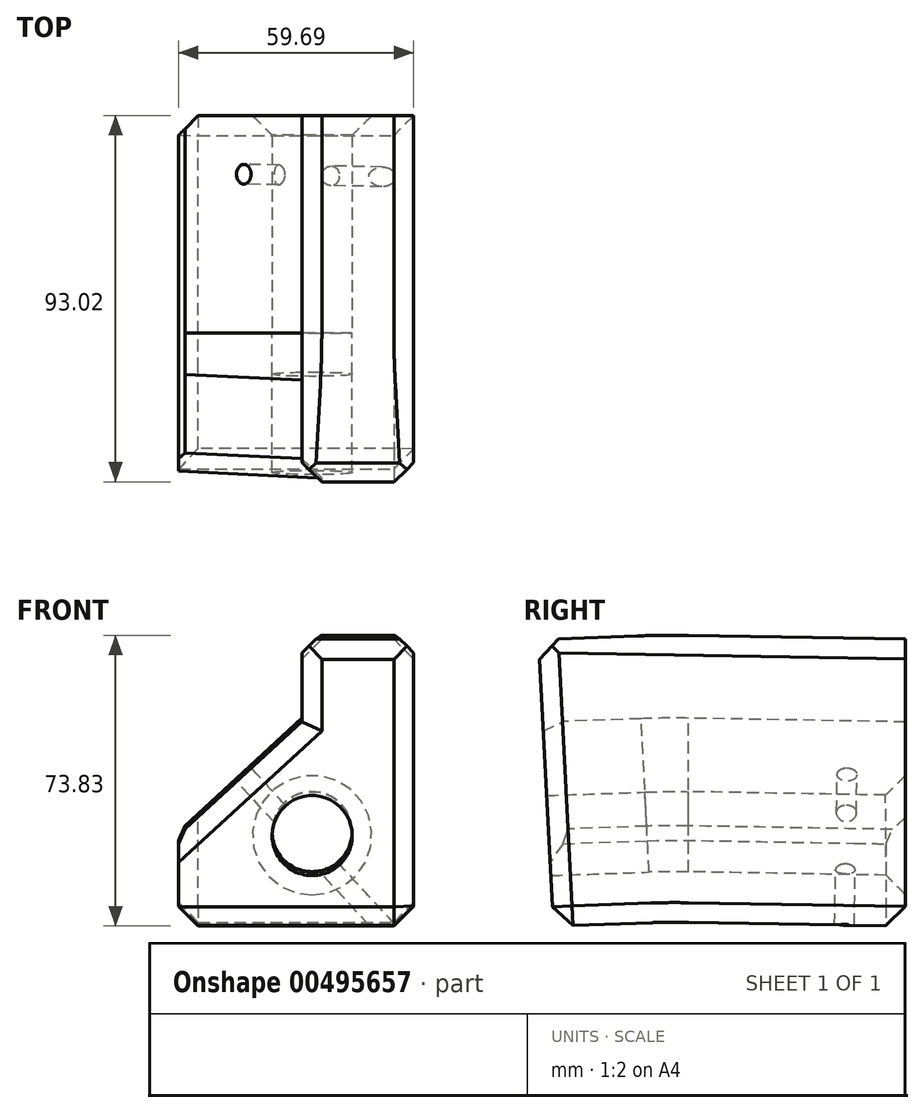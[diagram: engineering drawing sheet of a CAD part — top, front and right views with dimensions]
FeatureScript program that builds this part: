
annotation { "Feature Type Name" : "Feature", "Feature Type Description" : "" }
export const myFeature = defineFeature(function(context is Context, id is Id, definition is map)
    precondition{}
    {
        {
            var Q0;
            Q0=qCreatedBy(makeId("Front.planeOp"),FACE);
            var sketch = newSketch(context, id + "F0", { "sketchPlane" : qUnion([Q0])});
            skLineSegment(sketch, "E0", {"start": v(0, 0) * mm, "end": v(31.39, 28.85) * mm});
            skLineSegment(sketch, "E1", {"start": v(31.39, 28.85) * mm, "end": v(31.39, 49.9) * mm});
            skLineSegment(sketch, "E2", {"start": v(31.39, 49.9) * mm, "end": v(59.69, 49.9) * mm});
            skLineSegment(sketch, "E3", {"start": v(59.69, 49.9) * mm, "end": v(59.69, -23.04) * mm});
            skLineSegment(sketch, "E4", {"start": v(59.69, -23.04) * mm, "end": v(0, -23.04) * mm});
            skLineSegment(sketch, "E5", {"start": v(0, -23.04) * mm, "end": v(0, 0) * mm});
            skCircle(sketch, "E6", {"center": v(33.93, 0) * mm, "radius": 10.17 * mm});
            skSolve(sketch);
        }
        {
            var Q0;
            Q0=qCreatedBy(makeId("Right.planeOp"),FACE);
            var sketch = newSketch(context, id + "F1", { "sketchPlane" : qUnion([Q0])});
            skLineSegment(sketch, "E7", {"start": v(0, 0) * mm, "end": v(-55.22, 0.96) * mm});
            skLineSegment(sketch, "E8", {"start": v(-65.69, 0.87) * mm, "end": v(-90.67, 0) * mm});
            skPoint(sketch, "E9.visualSharp", {"position": v(-60.46, 1.06) * mm});
            skArc(sketch, "E9.filletArc", {"start": v(-55.22, 0.96) * mm, "mid": v(-60.46, 0.99) * mm, "end": v(-65.69, 0.87) * mm});
            skSolve(sketch);
        }
        {
            var Q0;
            Q0=makeQuery(id+"F0.imprint","IMPRINT",FACE,{"disambiguationData":[TD([[makeQuery(id+"F0.imprint","IMPRINT",EDGE,{"derivedFrom":sQuery(id+"F0.wireOp",EDGE,"E0")}),-1.0]])]});
            var Q1;
            Q1 = qConstructionFilter(qBodyType(qCreatedBy(id + "F1" ,EDGE), BodyType.WIRE), ConstructionObject.NO);
            sweep(context, id + "F2", {"profiles" : qUnion([Q0]), "path" : qUnion([Q1])});
        }
        {
            var Q0;
            Q0=makeQuery(id+"F2.opSweep","SWEPT_FACE",FACE,{"disambiguationData":[OSD([sQuery(id+"F0.wireOp",EDGE,"E5"),sQuery(id+"F1.wireOp",EDGE,"E7")])]});
            var sketch = newSketch(context, id + "F3", { "sketchPlane" : qUnion([Q0])});
            skCircle(sketch, "E10", {"center": v(22.5, -15.15) * mm, "radius": 2.5 * mm});
            skSolve(sketch);
        }
        {
            var Q0;
            Q0=makeQuery(id+"F3.imprint","IMPRINT",FACE,{"disambiguationData":[TD([[makeQuery(id+"F3.imprint","IMPRINT",EDGE,{"derivedFrom":sQuery(id+"F3.wireOp",EDGE,"E10")}),1.0]])]});
            extrude(context, id + "F4", {"entities" : qUnion([Q0]), "operationType" : NewBodyOperationType.REMOVE, "oppositeDirection" : true, "depth" : 200 * mm});
        }
        {
            var Q0;
            Q0=makeQuery(id+"F2.opSweep","SWEPT_EDGE",EDGE,{"disambiguationData":[OSD([sQuery(id+"F0.wireOp",EDGE,"E1"),sQuery(id+"F0.wireOp",EDGE,"E2"),sQuery(id+"F1.wireOp",EDGE,"E7")])]});
            var Q1;
            Q1=makeQuery(id+"F2.opSweep","SWEPT_EDGE",EDGE,{"disambiguationData":[OSD([sQuery(id+"F0.wireOp",EDGE,"E0"),sQuery(id+"F0.wireOp",EDGE,"E5"),sQuery(id+"F1.wireOp",EDGE,"E8")])]});
            var Q2;
            Q2=makeQuery(id+"F2.opSweep","SWEPT_EDGE",EDGE,{"disambiguationData":[OSD([sQuery(id+"F0.wireOp",EDGE,"E2"),sQuery(id+"F0.wireOp",EDGE,"E3"),sQuery(id+"F1.wireOp",EDGE,"E7")])]});
            var Q3;
            Q3=makeQuery(id+"F2.opSweep","SWEPT_EDGE",EDGE,{"disambiguationData":[OSD([sQuery(id+"F0.wireOp",EDGE,"E4"),sQuery(id+"F0.wireOp",EDGE,"E5"),sQuery(id+"F1.wireOp",EDGE,"E8")])]});
            var Q4;
            Q4=makeQuery(id+"F2.opSweep","SWEPT_EDGE",EDGE,{"disambiguationData":[OSD([sQuery(id+"F0.wireOp",EDGE,"E3"),sQuery(id+"F0.wireOp",EDGE,"E4"),sQuery(id+"F1.wireOp",EDGE,"E8")])]});
            var Q5;
            Q5=makeQuery(id+"F2.opSweep","SWEPT_EDGE",EDGE,{"disambiguationData":[OSD([sQuery(id+"F0.wireOp",EDGE,"E3"),sQuery(id+"F0.wireOp",EDGE,"E4"),sQuery(id+"F1.wireOp",EDGE,"E7")])]});
            var Q6;
            Q6=makeQuery(id+"F2.opSweep","CAP_EDGE",EDGE,{"disambiguationData":[OSD([sQuery(id+"F0.wireOp",EDGE,"E3"),sQuery(id+"F1.wireOp",VERTEX,"E8.end")])],"isStart":false});
            var Q7;
            Q7=makeQuery(id+"F2.opSweep","CAP_EDGE",EDGE,{"disambiguationData":[OSD([sQuery(id+"F0.wireOp",EDGE,"E4"),sQuery(id+"F1.wireOp",VERTEX,"E8.end")])],"isStart":false});
            var Q8;
            Q8=makeQuery(id+"F2.opSweep","CAP_EDGE",EDGE,{"disambiguationData":[OSD([sQuery(id+"F0.wireOp",EDGE,"E2"),sQuery(id+"F1.wireOp",VERTEX,"E8.end")])],"isStart":false});
            var Q9;
            Q9=makeQuery(id+"F2.opSweep","CAP_EDGE",EDGE,{"disambiguationData":[OSD([sQuery(id+"F0.wireOp",EDGE,"E1"),sQuery(id+"F1.wireOp",VERTEX,"E8.end")])],"isStart":false});
            var Q10;
            Q10=makeQuery(id+"F2.opSweep","CAP_EDGE",EDGE,{"disambiguationData":[OSD([sQuery(id+"F0.wireOp",EDGE,"E0"),sQuery(id+"F1.wireOp",VERTEX,"E8.end")])],"isStart":false});
            var Q11;
            Q11=makeQuery(id+"F2.opSweep","SWEPT_EDGE",EDGE,{"disambiguationData":[OSD([sQuery(id+"F0.wireOp",EDGE,"E4"),sQuery(id+"F0.wireOp",EDGE,"E5"),sQuery(id+"F1.wireOp",EDGE,"E7")])]});
            var Q12;
            Q12=makeQuery(id+"F2.opSweep","CAP_EDGE",EDGE,{"disambiguationData":[OSD([sQuery(id+"F0.wireOp",EDGE,"E4"),sQuery(id+"F1.wireOp",VERTEX,"E7.start")])],"isStart":true});
            var Q13;
            Q13=makeQuery(id+"F2.opSweep","CAP_EDGE",EDGE,{"disambiguationData":[OSD([sQuery(id+"F0.wireOp",EDGE,"E5"),sQuery(id+"F1.wireOp",VERTEX,"E7.start")])],"isStart":true});
            var Q14;
            Q14=makeQuery(id+"F4.boolean.opBoolean","COPY",EDGE,{"derivedFrom":makeQuery(id+"F4.opExtrude","CAP_EDGE",EDGE,{"disambiguationData":[OSD([sQuery(id+"F3.wireOp",EDGE,"E10")])],"isStart":true})});
            var Q15;
            Q15=makeQuery(id+"F2.opSweep","CAP_EDGE",EDGE,{"disambiguationData":[OSD([sQuery(id+"F0.wireOp",EDGE,"E6"),sQuery(id+"F1.wireOp",VERTEX,"E7.start")])],"isStart":true});
            chamfer(context, id + "F5", {"entities" : qUnion([Q0, Q1, Q2, Q3, Q4, Q5, Q6, Q7, Q8, Q9, Q10, Q11, Q12, Q13, Q14, Q15]), "width" : 5 * mm, "tangentPropagation" : true});
        }
    });
